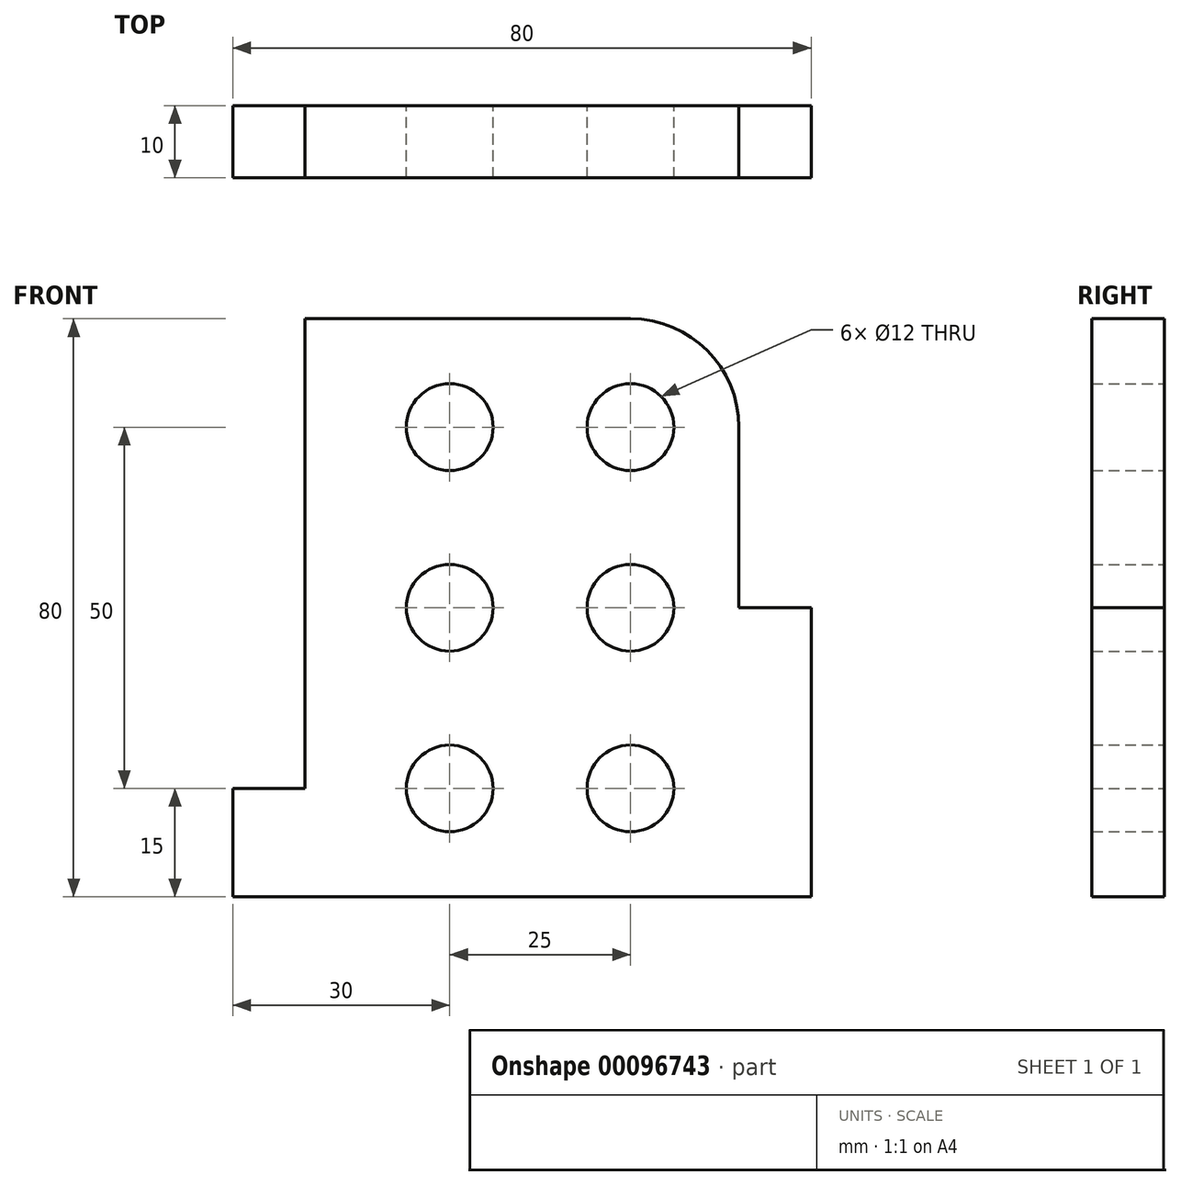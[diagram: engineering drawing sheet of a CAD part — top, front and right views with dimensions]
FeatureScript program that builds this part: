
annotation { "Feature Type Name" : "Feature", "Feature Type Description" : "" }
export const myFeature = defineFeature(function(context is Context, id is Id, definition is map)
    precondition{}
    {
        {
            var Q0;
            Q0=qCreatedBy(makeId("Front.planeOp"),FACE);
            var sketch = newSketch(context, id + "F0", { "sketchPlane" : qUnion([Q0])});
            skLineSegment(sketch, "E0", {"start": v(0, 0) * mm, "end": v(0, 15) * mm});
            skLineSegment(sketch, "E1", {"start": v(0, 15) * mm, "end": v(10, 15) * mm});
            skLineSegment(sketch, "E2", {"start": v(10, 15) * mm, "end": v(10, 80) * mm});
            skLineSegment(sketch, "E3", {"start": v(0, 0) * mm, "end": v(80, 0) * mm});
            skLineSegment(sketch, "E4", {"start": v(80, 0) * mm, "end": v(80, 40) * mm});
            skLineSegment(sketch, "E5", {"start": v(80, 40) * mm, "end": v(70, 40) * mm});
            skLineSegment(sketch, "E6", {"start": v(70, 40) * mm, "end": v(70, 65) * mm});
            skCircle(sketch, "E7", {"center": v(55, 65) * mm, "radius": 6 * mm});
            skCircle(sketch, "E8", {"center": v(30, 65) * mm, "radius": 6 * mm});
            skCircle(sketch, "E9", {"center": v(30, 40) * mm, "radius": 6 * mm});
            skCircle(sketch, "E10", {"center": v(55, 40) * mm, "radius": 6 * mm});
            skCircle(sketch, "E11", {"center": v(30, 15) * mm, "radius": 6 * mm});
            skCircle(sketch, "E12", {"center": v(55, 15) * mm, "radius": 6 * mm});
            skLineSegment(sketch, "E13", {"start": v(10, 80) * mm, "end": v(55, 80) * mm});
            skArc(sketch, "E14", {"start": v(70, 65) * mm, "mid": v(65.6, 75.6) * mm, "end": v(55, 80) * mm});
            skLineSegment(sketch, "E15", {"start": v(30, 65) * mm, "end": v(30, 15) * mm, "construction": true});
            skLineSegment(sketch, "E16", {"start": v(30, 65) * mm, "end": v(55, 65) * mm, "construction": true});
            skLineSegment(sketch, "E17", {"start": v(55, 65) * mm, "end": v(55, 15) * mm, "construction": true});
            skLineSegment(sketch, "E18", {"start": v(55, 15) * mm, "end": v(30, 15) * mm, "construction": true});
            skLineSegment(sketch, "E19", {"start": v(55, 40) * mm, "end": v(30, 40) * mm, "construction": true});
            skSolve(sketch);
        }
        {
            var Q0;
            Q0 = qSketchRegion(id + "F0", true);
            extrude(context, id + "F1", {"entities" : qUnion([Q0]), "depth" : 10 * mm});
        }
    });
